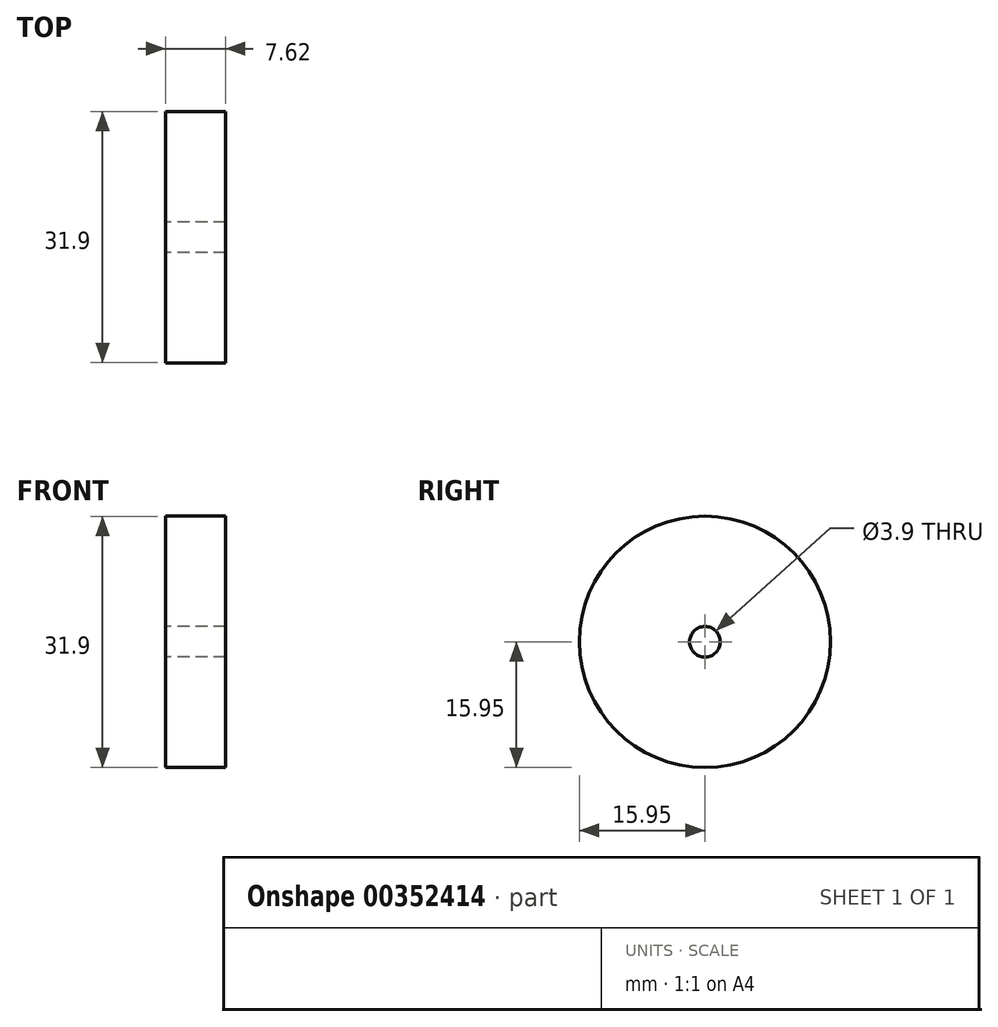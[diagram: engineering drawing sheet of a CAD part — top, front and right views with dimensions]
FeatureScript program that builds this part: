
annotation { "Feature Type Name" : "Feature", "Feature Type Description" : "" }
export const myFeature = defineFeature(function(context is Context, id is Id, definition is map)
    precondition{}
    {
        {
            var Q0;
            Q0=qCreatedBy(makeId("Right.planeOp"),FACE);
            var sketch = newSketch(context, id + "F0", { "sketchPlane" : qUnion([Q0])});
            skCircle(sketch, "E0", {"center": v(0, 0) * mm, "radius": 15.95 * mm});
            skSolve(sketch);
        }
        {
            var Q0;
            Q0=makeQuery(id+"F0.imprint","IMPRINT",FACE,{"disambiguationData":[TD([[makeQuery(id+"F0.imprint","IMPRINT",EDGE,{"derivedFrom":sQuery(id+"F0.wireOp",EDGE,"E0")}),1.0]])]});
            extrude(context, id + "F1", {"entities" : qUnion([Q0]), "depth" : 7.62 * mm});
        }
        {
            var Q0;
            Q0=makeQuery(id+"F1.opExtrude","CAP_FACE",FACE,{"disambiguationData":[OSD([sQuery(id+"F0.wireOp",EDGE,"E0")])],"isStart":true});
            var sketch = newSketch(context, id + "F2", { "sketchPlane" : qUnion([Q0])});
            skCircle(sketch, "E1", {"center": v(0, 0) * mm, "radius": 1.95 * mm});
            skSolve(sketch);
        }
        {
            var Q0;
            Q0=makeQuery(id+"F2.imprint","IMPRINT",FACE,{"disambiguationData":[TD([[makeQuery(id+"F2.imprint","IMPRINT",EDGE,{"derivedFrom":sQuery(id+"F2.wireOp",EDGE,"E1")}),1.0]])]});
            extrude(context, id + "F3", {"entities" : qUnion([Q0]), "operationType" : NewBodyOperationType.REMOVE, "oppositeDirection" : true, "depth" : 25.4 * mm});
        }
    });
